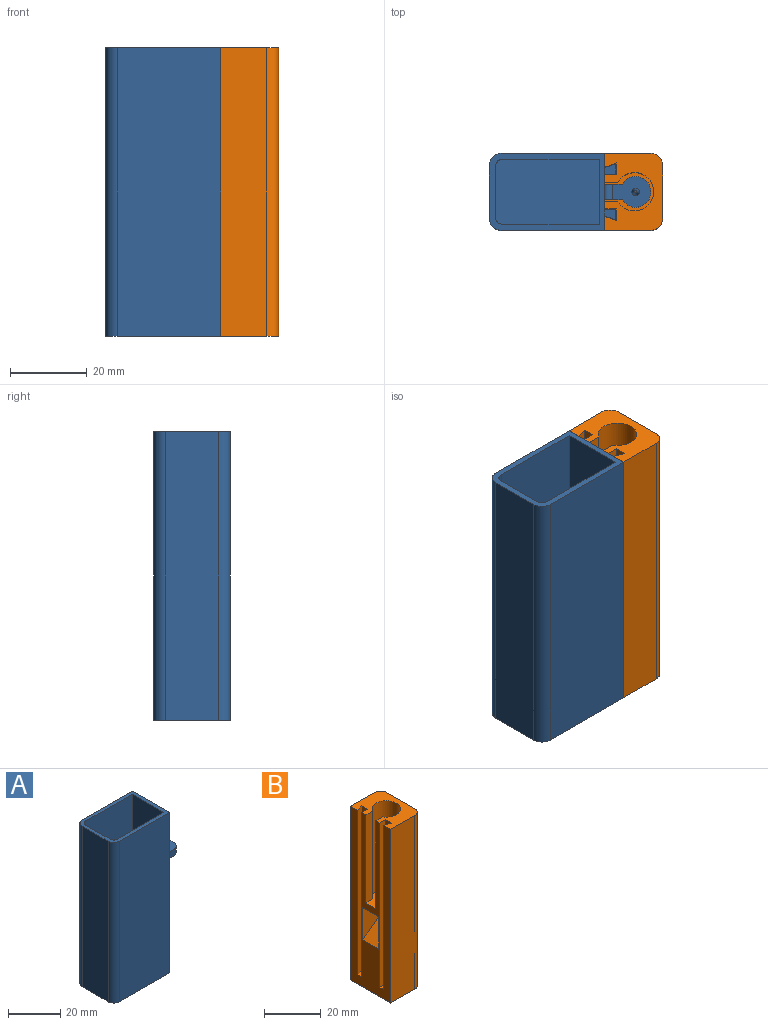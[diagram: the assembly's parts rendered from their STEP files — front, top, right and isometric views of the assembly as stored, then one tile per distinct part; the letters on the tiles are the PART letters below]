
ASSEMBLY  parts=2 mates=1
PART A: 43 faces, bbox 42x20x75 mm
  f0: plane 4.7x4mm, normal (0.6,0,-0.8), area 23.4mm2, adj f1,f2,f39,f42
  f1: plane 12.51x6.71mm, normal (0,-1,0), area 32.2mm2, adj f0,f3,f36,f37,f38,f39,f42
  f2: plane 12.51x6.71mm, normal (0,1,0), area 32.2mm2, adj f0,f3,f36,f37,f38,f39,f42
  f3: plane 75x20mm, normal (1,0,0), area 1041.1mm2, adj f1,f2,f5,f6,f7,f11,f18,f19
  f4: plane 55x17mm, normal (-1,0,0), area 823mm2, adj f6,f12,f16,f17,f22,f23,f24,f25
  f5: plane 30x20mm, normal (0,0,-1), area 491.4mm2, adj f3,f7,f8,f9,f10,f11,f18,f19
  f6: plane 30x20mm, normal (0,0,1), area 138.9mm2, adj f3,f4,f7,f8,f9,f10,f11,f12
  f7: plane 75x27mm, normal (0,1,0), area 2025mm2, adj f3,f5,f6,f8
  f8: cylinder r=3mm len=75mm, axis (0,0,-1), area 353.4mm2, adj f5,f6,f7,f9
  f9: plane 75x14mm, normal (-1,0,0), area 1050mm2, adj f5,f6,f8,f10
  f10: cylinder r=3mm len=75mm, axis (0,0,-1), area 353.4mm2, adj f5,f6,f9,f11
  f11: plane 75x27mm, normal (0,-1,0), area 2025mm2, adj f3,f5,f6,f10
  f12: plane 55x25mm, normal (0,-1,0), area 1375mm2, adj f4,f6,f13,f17
  f13: cylinder r=2mm len=55mm, axis (0,0,1), area 172.8mm2, adj f6,f12,f14,f17
  f14: plane 55x13mm, normal (1,0,0), area 715mm2, adj f6,f13,f15,f17
  f15: cylinder r=2mm len=55mm, axis (0,0,1), area 172.8mm2, adj f6,f14,f16,f17
  f16: plane 55x25mm, normal (0,1,0), area 1375mm2, adj f4,f6,f15,f17
  f17: plane 27x17mm, normal (0,0,1), area 457.3mm2, adj f4,f12,f13,f14,f15,f16
  f18: plane 23.48x19mm, normal (0.63,0,-0.78), area 226.3mm2, adj f3,f5,f19,f21
  f19: bspline ~23.48x19mm, area 202.1mm2, adj f3,f5,f18,f20
  f20: plane 8.48x8mm, normal (-0.51,0,0.86), area 73.7mm2, adj f3,f5,f19,f21
  f21: bspline ~23.48x19mm, area 201.9mm2, adj f3,f5,f18,f20
  f22: plane 8x1.5mm, normal (0,0,-1), area 12mm2, adj f3,f4,f23,f25
  f23: plane 14x1.5mm, normal (0,1,0), area 21mm2, adj f3,f4,f22,f24
  f24: plane 8x1.5mm, normal (0,0,1), area 12mm2, adj f3,f4,f23,f25
  f25: plane 14x1.5mm, normal (0,-1,0), area 21mm2, adj f3,f4,f22,f24
  f26: plane 2.8x2.7mm, normal (0,0,-1), area 6.1mm2, adj f3,f27,f29,f30
  f27: plane 55x2.8mm, normal (0,1,0), area 154mm2, adj f3,f26,f28,f29
  f28: plane 2.8x2.7mm, normal (0,0,1), area 6.1mm2, adj f3,f27,f29,f30
  f29: plane 55x2.7mm, normal (1,0,0), area 148.5mm2, adj f26,f27,f28,f30
  f30: plane 55x2.8mm, normal (-0.34,-0.94,0), area 163.9mm2, adj f3,f26,f28,f29
  f31: plane 2.8x2.7mm, normal (0,0,-1), area 6.1mm2, adj f3,f32,f34,f35
  f32: plane 55x2.8mm, normal (0,-1,0), area 154mm2, adj f3,f31,f33,f34
  f33: plane 2.8x2.7mm, normal (0,0,1), area 6.1mm2, adj f3,f32,f34,f35
  f34: plane 55x2.7mm, normal (1,0,0), area 148.5mm2, adj f31,f32,f33,f35
  f35: plane 55x2.8mm, normal (-0.34,0.94,0), area 163.9mm2, adj f3,f31,f33,f34
  f36: plane 10x8mm, normal (0,0,1), area 55.9mm2, adj f1,f2,f37,f38,f40
  f37: cylinder r=2mm len=4mm, axis (0,-1,0), area 12.6mm2, adj f1,f2,f3,f36
  f38: cylinder r=4mm len=8mm, axis (0,0,1), area 62.8mm2, adj f1,f2,f36,f39
  f39: plane 8x7.46mm, normal (0,0,-1), area 40.1mm2, adj f0,f1,f2,f38
  f40: cone r=0.98mm half-angle=13deg, axis (0,0,-1), area 12.3mm2, adj f36,f41
  f41: plane 0.57x0.57mm, normal (0,0,1), area 0.3mm2, adj f40
  f42: cylinder r=5mm len=4.01mm, axis (0,1,0), area 18.6mm2, adj f0,f1,f2,f3
PART B: 25 faces, bbox 15x20x75 mm
  f0: plane 75x20mm, normal (-1,0,0), area 927.1mm2, adj f1,f3,f4,f8,f9,f10,f11,f12
  f1: plane 14x12mm, normal (0,1,0), area 92.4mm2, adj f0,f2,f10,f11
  f2: plane 8x1.4mm, normal (-1,0,0), area 11.2mm2, adj f1,f9,f10,f11
  f3: plane 75x12mm, normal (0,1,0), area 900mm2, adj f0,f7,f8,f24
  f4: plane 75x12mm, normal (0,-1,0), area 900mm2, adj f0,f5,f8,f24
  f5: cylinder r=3mm len=75mm, axis (0,0,-1), area 353.4mm2, adj f4,f6,f8,f24
  f6: plane 75x14mm, normal (1,0,0), area 1050mm2, adj f5,f7,f8,f24
  f7: cylinder r=3mm len=75mm, axis (0,0,-1), area 353.4mm2, adj f3,f6,f8,f24
  f8: plane 20x15mm, normal (0,0,-1), area 296.1mm2, adj f0,f3,f4,f5,f6,f7
  f9: plane 14x12mm, normal (0,-1,0), area 92.4mm2, adj f0,f2,f10,f11
  f10: plane 12x8.96mm, normal (-0.6,0,0.8), area 119.8mm2, adj f0,f1,f2,f9
  f11: plane 12x8mm, normal (-0.29,0,-0.96), area 100.3mm2, adj f0,f1,f2,f9
  f12: plane 71x3mm, normal (0,-1,0), area 213mm2, adj f0,f14,f15,f24
  f13: plane 71x3mm, normal (0.34,0.94,0), area 226.7mm2, adj f0,f14,f15,f24
  f14: plane 71x3mm, normal (-1,0,0), area 213mm2, adj f12,f13,f15,f24
  f15: plane 3x3mm, normal (0,0,1), area 7.4mm2, adj f0,f12,f13,f14
  f16: plane 71x3mm, normal (0,1,0), area 213mm2, adj f0,f17,f19,f24
  f17: plane 71x3mm, normal (-1,0,0), area 213mm2, adj f16,f18,f19,f24
  f18: plane 71x3mm, normal (0.34,-0.94,0), area 226.7mm2, adj f0,f17,f19,f24
  f19: plane 3x3mm, normal (0,0,1), area 7.4mm2, adj f0,f16,f17,f18
  f20: cylinder r=5mm len=38mm, axis (0,0,1), area 994.8mm2, adj f21,f22,f23,f24
  f21: plane 12.73x10mm, normal (0,0,1), area 93.3mm2, adj f0,f20,f22,f23
  f22: plane 38x3.4mm, normal (0,1,0), area 129.3mm2, adj f0,f20,f21,f24
  f23: plane 38x3.4mm, normal (0,-1,0), area 129.3mm2, adj f0,f20,f21,f24
  f24: plane 20x15mm, normal (0,0,1), area 188.1mm2, adj f0,f3,f4,f5,f6,f7,f12,f13
PLACE A at identity
PLACE B t=(8.91,17.52,0)mm
MATE fastened B.f0 <-> A.f3  axis (-1,0,0) through (19.25,-15.14,0)mm
